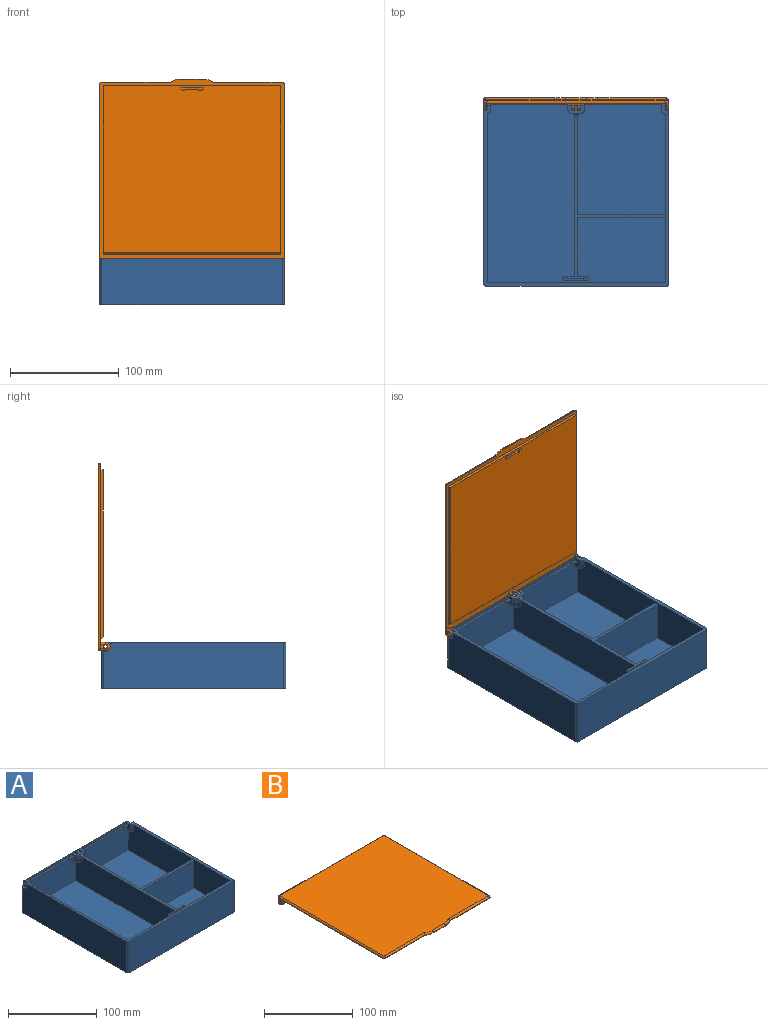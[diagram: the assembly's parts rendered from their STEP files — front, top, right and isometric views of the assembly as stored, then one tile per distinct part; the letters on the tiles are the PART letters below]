
ASSEMBLY  parts=2 mates=1
PART A: 141 faces, bbox 170x170x43 mm
  f0: plane 71.5x2.44mm, normal (0,-1,0), area 170.4mm2, adj f4,f5,f25,f28,f56,f59,f129,f130
  f1: plane 71.5x2.44mm, normal (0,-1,0), area 170.4mm2, adj f6,f7,f26,f27,f57,f60,f125,f126
  f2: plane 80.5x34.56mm, normal (0,-1,0), area 2726.1mm2, adj f4,f5,f25,f28,f32,f34,f44,f56
  f3: plane 80.5x34.56mm, normal (0,-1,0), area 2726.1mm2, adj f6,f7,f26,f27,f33,f39,f43,f57
  f4: cylinder r=1.75mm len=6mm, axis (1,0,0), area 43.1mm2, adj f0,f2,f21,f28,f132
  f5: cylinder r=1.75mm len=61.5mm, axis (1,0,0), area 207.2mm2, adj f0,f2,f130,f131
  f6: cylinder r=1.75mm len=61.5mm, axis (1,0,0), area 207.2mm2, adj f1,f3,f125,f127
  f7: cylinder r=1.75mm len=6mm, axis (1,0,0), area 43.1mm2, adj f1,f3,f22,f26,f126
  f8: plane 9x4mm, normal (0,1,0), area 31.6mm2, adj f13,f15,f38,f100,f101,f102,f105,f106
  f9: plane 20.6x4mm, normal (0,-1,0), area 79.4mm2, adj f11,f12,f15,f90,f91,f92,f96,f97
  f10: plane 20.6x4mm, normal (0,1,0), area 79.4mm2, adj f11,f12,f15,f90,f91,f92,f95,f96
  f11: plane 3.3x1.8mm, normal (0,0,1), area 5.9mm2, adj f9,f10,f90,f98
  f12: plane 11x1.8mm, normal (0,0,1), area 19.8mm2, adj f9,f10,f96,f100
  f13: plane 4.54x4.54mm, normal (0,0.71,-0.71), area 25.7mm2, adj f8,f38,f100,f109
  f14: plane 3.95x3.95mm, normal (0,0.71,-0.71), area 19.6mm2, adj f98,f104,f110,f122,f123
  f15: plane 153.04x95.5mm, normal (0,0,1), area 794.3mm2, adj f8,f9,f10,f16,f32,f34,f38,f39
  f16: plane 164x40mm, normal (0,1,0), area 6185mm2, adj f15,f19,f32,f33,f37,f38,f39,f43
  f17: plane 8.25x8.25mm, normal (1,0,0), area 51.4mm2, adj f20,f31,f36,f51,f54,f58,f61
  f18: plane 8.25x8.25mm, normal (-1,0,0), area 51.4mm2, adj f20,f29,f30,f36,f55,f58,f61
  f19: plane 170x166.13mm, normal (0,0,1), area 1503.5mm2, adj f16,f21,f24,f27,f28,f32,f33,f35
  f20: plane 15x7.13mm, normal (0,0,1), area 76.8mm2, adj f17,f18,f22,f23,f25,f26,f29,f51
  f21: plane 8.25x8.25mm, normal (1,0,0), area 51.4mm2, adj f4,f19,f36,f47,f48,f53,f59
  f22: plane 8.25x8.25mm, normal (1,0,0), area 51.4mm2, adj f7,f20,f29,f30,f36,f55,f60
  f23: plane 8.25x8.25mm, normal (-1,0,0), area 51.4mm2, adj f20,f31,f36,f51,f54,f56,f59
  f24: plane 8.25x8.25mm, normal (-1,0,0), area 51.4mm2, adj f19,f36,f49,f50,f52,f57,f60
  f25: plane 8.25x5mm, normal (1,0,0), area 29.7mm2, adj f0,f2,f20,f56,f59,f80,f82,f84
  f26: plane 8.25x5mm, normal (-1,0,0), area 29.7mm2, adj f1,f3,f7,f20,f60,f74,f76,f77
  f27: plane 9.75x6.5mm, normal (1,0,0), area 48.7mm2, adj f1,f3,f19,f57,f60,f64,f66,f67
  f28: plane 9.75x6.5mm, normal (-1,0,0), area 48.7mm2, adj f0,f2,f4,f19,f59,f68,f70,f71
  f29: plane 4.15x3mm, normal (0,1,0), area 12.4mm2, adj f18,f20,f22,f55
  f30: plane 4.15x3mm, normal (0,0,1), area 12.5mm2, adj f18,f22,f36,f55
  f31: plane 4.15x3mm, normal (0,0,1), area 12.5mm2, adj f17,f23,f36,f54
  f32: plane 164x40mm, normal (-1,0,0), area 6341.9mm2, adj f2,f15,f16,f19,f37,f44,f45,f46
  f33: plane 164x40mm, normal (1,0,0), area 6454.4mm2, adj f3,f16,f19,f43,f62,f63,f65
  f34: plane 101x37.5mm, normal (1,0,0), area 3679.7mm2, adj f2,f15,f44,f46,f81,f83,f85
  f35: plane 166x43mm, normal (-1,0,0), area 7090mm2, adj f19,f42,f49,f50,f52,f113,f116
  f36: plane 166x39.13mm, normal (0,1,0), area 6459.8mm2, adj f17,f18,f21,f22,f23,f24,f30,f31
  f37: plane 80.5x60mm, normal (0,0,1), area 4830mm2, adj f16,f32,f38,f45
  f38: plane 60x37.5mm, normal (1,0,0), area 2207.5mm2, adj f8,f13,f15,f16,f37,f45,f109
  f39: plane 164x37.5mm, normal (-1,0,0), area 5999.7mm2, adj f3,f15,f16,f43,f75,f78,f79,f88
  f40: plane 166x43mm, normal (0,-1,0), area 7138mm2, adj f19,f42,f113,f114
  f41: plane 166x43mm, normal (1,0,0), area 7090mm2, adj f19,f42,f47,f48,f53,f114,f115
  f42: plane 170x170mm, normal (0,0,-1), area 28896.6mm2, adj f35,f36,f40,f41,f113,f114,f115,f116
  f43: plane 164x80.5mm, normal (0,0,1), area 13202mm2, adj f3,f16,f33,f39
  f44: plane 101x80.5mm, normal (0,0,1), area 8130.5mm2, adj f2,f32,f34,f46
  f45: plane 80.5x37.5mm, normal (0,-1,0), area 3018.8mm2, adj f15,f32,f37,f38
  f46: plane 80.5x37.5mm, normal (0,1,0), area 3018.8mm2, adj f15,f32,f34,f44
  f47: plane 4.15x3mm, normal (0,0,1), area 11.6mm2, adj f21,f36,f41,f53,f115
  f48: plane 4.15x3mm, normal (0,1,0), area 12.4mm2, adj f19,f21,f41,f53
  f49: plane 4.15x3mm, normal (0,1,0), area 12.4mm2, adj f19,f24,f35,f52
  f50: plane 4.15x3mm, normal (0,0,1), area 11.6mm2, adj f24,f35,f36,f52,f116
  f51: plane 4.15x3mm, normal (0,1,0), area 12.4mm2, adj f17,f20,f23,f54
  f52: cylinder r=4.1mm len=4.1mm, axis (1,0,0), area 19.3mm2, adj f24,f35,f49,f50
  f53: cylinder r=4.1mm len=4.1mm, axis (1,0,0), area 19.3mm2, adj f21,f41,f47,f48
  f54: cylinder r=4.1mm len=4.1mm, axis (-1,0,0), area 19.3mm2, adj f17,f23,f31,f51
  f55: cylinder r=4.1mm len=4.1mm, axis (-1,0,0), area 19.3mm2, adj f18,f22,f29,f30
  f56: cylinder r=1.75mm len=6mm, axis (1,0,0), area 43.1mm2, adj f0,f2,f23,f25,f129
  f57: cylinder r=1.75mm len=6mm, axis (1,0,0), area 43.1mm2, adj f1,f3,f24,f27,f128
  f58: cylinder r=1.75mm len=3.5mm, axis (1,0,0), area 33mm2, adj f17,f18
  f59: cylinder r=4mm len=77.5mm, axis (-1,0,0), area 404.5mm2, adj f0,f19,f20,f21,f23,f25,f28,f36
  f60: cylinder r=4mm len=77.5mm, axis (-1,0,0), area 404.5mm2, adj f1,f19,f20,f22,f24,f26,f27,f36
  f61: cylinder r=4mm len=3.88mm, axis (-1,0,0), area 18.1mm2, adj f17,f18,f20,f36
  f62: cylinder r=1.5mm len=4.25mm, axis (0,0,-1), area 10mm2, adj f19,f33,f63,f64
  f63: torus R=8.5mm, axis (-1,0,0), area 27.9mm2, adj f33,f62,f65,f66
  f64: cylinder r=1.5mm len=4.25mm, axis (0,0,-1), area 10mm2, adj f19,f27,f62,f66
  f65: cylinder r=1.5mm len=1.5mm, axis (0,-1,0), area 2.4mm2, adj f3,f33,f63,f67
  f66: torus R=5.5mm, axis (1,0,0), area 23.9mm2, adj f27,f63,f64,f67
  f67: cylinder r=1.5mm len=1.5mm, axis (0,-1,0), area 2.4mm2, adj f3,f27,f65,f66
  f68: cylinder r=1.5mm len=1.5mm, axis (0,-1,0), area 2.4mm2, adj f2,f28,f69,f70
  f69: cylinder r=1.5mm len=1.5mm, axis (0,1,0), area 2.4mm2, adj f2,f32,f68,f72
  f70: torus R=5.5mm, axis (-1,0,0), area 23.9mm2, adj f28,f68,f71,f72
  f71: cylinder r=1.5mm len=4.25mm, axis (0,0,1), area 10mm2, adj f19,f28,f70,f73
  f72: torus R=8.5mm, axis (-1,0,0), area 27.9mm2, adj f32,f69,f70,f73
  f73: cylinder r=1.5mm len=4.25mm, axis (0,0,1), area 10mm2, adj f19,f32,f71,f72
  f74: cylinder r=3mm len=3mm, axis (0,1,0), area 4.7mm2, adj f3,f26,f75,f76
  f75: cylinder r=3mm len=3mm, axis (0,-1,0), area 4.7mm2, adj f3,f39,f74,f78
  f76: torus R=4mm, axis (-1,0,0), area 43.7mm2, adj f26,f74,f77,f78
  f77: cylinder r=3mm len=4.25mm, axis (0,0,1), area 20mm2, adj f20,f26,f76,f79
  f78: torus R=10mm, axis (-1,0,0), area 59.9mm2, adj f39,f75,f76,f79
  f79: cylinder r=3mm len=4.25mm, axis (0,0,1), area 13mm2, adj f15,f39,f77,f78,f86
  f80: cylinder r=3mm len=4.25mm, axis (0,0,-1), area 20mm2, adj f20,f25,f81,f82
  f81: cylinder r=3mm len=4.25mm, axis (0,0,-1), area 13mm2, adj f15,f34,f80,f83,f86
  f82: torus R=4mm, axis (-1,0,0), area 43.7mm2, adj f25,f80,f83,f84
  f83: torus R=10mm, axis (-1,0,0), area 59.9mm2, adj f34,f81,f82,f85
  f84: cylinder r=3mm len=3mm, axis (0,1,0), area 4.7mm2, adj f2,f25,f82,f85
  f85: cylinder r=3mm len=3mm, axis (0,-1,0), area 4.7mm2, adj f2,f34,f83,f84
  f86: cylinder r=3mm len=9mm, axis (-1,0,0), area 20.6mm2, adj f15,f20,f79,f81
  f87: plane 6.17x3mm, normal (-1,0,0), area 14mm2, adj f15,f103,f108,f123
  f88: plane 9x4mm, normal (0,1,0), area 31.6mm2, adj f15,f39,f94,f96,f97,f98,f103,f104
  f89: plane 6.17x3mm, normal (1,0,0), area 14mm2, adj f15,f105,f107,f118
  f90: plane 4x1.8mm, normal (1,0,0), area 7.2mm2, adj f9,f10,f11,f15
  f91: plane 4x1.8mm, normal (-1,0,0), area 7.2mm2, adj f9,f10,f15,f92
  f92: plane 3.3x1.8mm, normal (0,0,1), area 5.9mm2, adj f9,f10,f91,f102
  f93: plane 3.95x3.95mm, normal (0,0.71,-0.71), area 19.6mm2, adj f102,f106,f112,f118,f119
  f94: plane 4.54x4.54mm, normal (0,0.71,-0.71), area 25.7mm2, adj f39,f88,f96,f111
  f95: plane 2.25x1.5mm, normal (0,0,-1), area 3.4mm2, adj f10,f16,f96,f98
  f96: plane 9.07x6mm, normal (-1,0,0), area 22.7mm2, adj f9,f10,f12,f16,f88,f94,f95,f97
  f97: plane 1.95x1.5mm, normal (0,0,-1), area 2.9mm2, adj f9,f88,f96,f98
  f98: plane 9.07x6mm, normal (1,0,0), area 22.7mm2, adj f9,f10,f11,f14,f16,f88,f95,f97
  f99: plane 2.25x1.5mm, normal (0,0,-1), area 3.4mm2, adj f10,f16,f100,f102
  f100: plane 9.07x6mm, normal (1,0,0), area 22.7mm2, adj f8,f9,f10,f12,f13,f16,f99,f101
  f101: plane 1.95x1.5mm, normal (0,0,-1), area 2.9mm2, adj f8,f9,f100,f102
  f102: plane 9.07x6mm, normal (-1,0,0), area 22.7mm2, adj f8,f9,f10,f16,f92,f93,f99,f101
  f103: cylinder r=2mm len=3.17mm, axis (0,0,-1), area 10mm2, adj f15,f87,f88,f124
  f104: cylinder r=2mm len=3.5mm, axis (-1,0,0), area 5.5mm2, adj f14,f88,f98,f124
  f105: cylinder r=2mm len=3.17mm, axis (0,0,1), area 10mm2, adj f8,f15,f89,f117
  f106: cylinder r=2mm len=3.5mm, axis (-1,0,0), area 5.5mm2, adj f8,f93,f102,f117
  f107: cylinder r=1mm len=12.07mm, axis (0,0,-1), area 14.1mm2, adj f15,f16,f89,f119,f120
  f108: cylinder r=1mm len=12.07mm, axis (0,0,1), area 14.1mm2, adj f15,f16,f87,f121,f122
  f109: cylinder r=5mm len=4mm, axis (1,0,0), area 15.7mm2, adj f13,f16,f38,f100
  f110: cylinder r=5mm len=6.5mm, axis (1,0,0), area 19.9mm2, adj f14,f16,f98,f121
  f111: cylinder r=5mm len=4mm, axis (1,0,0), area 15.7mm2, adj f16,f39,f94,f96
  f112: cylinder r=5mm len=6.5mm, axis (1,0,0), area 19.9mm2, adj f16,f93,f102,f120
  f113: cylinder r=2mm len=43mm, axis (0,0,1), area 135.1mm2, adj f19,f35,f40,f42
  f114: cylinder r=2mm len=43mm, axis (0,0,-1), area 135.1mm2, adj f19,f40,f41,f42
  f115: cylinder r=2mm len=34.75mm, axis (0,0,1), area 109.2mm2, adj f36,f41,f42,f47
  f116: cylinder r=2mm len=34.75mm, axis (0,0,-1), area 109.2mm2, adj f35,f36,f42,f50
  f117: sphere r=2mm, area 3.1mm2, adj f105,f106,f118
  f118: cylinder r=2mm len=4.41mm, axis (0,0.71,0.71), area 13.3mm2, adj f89,f93,f117,f119
  f119: bspline ~2.36x2.05mm, area 3.1mm2, adj f93,f107,f118,f120
  f120: bspline ~5.61x3mm, area 6.1mm2, adj f107,f112,f119
  f121: bspline ~5.44x2.98mm, area 5.4mm2, adj f108,f110,f122
  f122: bspline ~2.36x2.05mm, area 3.1mm2, adj f14,f108,f121,f123
  f123: cylinder r=2mm len=4.41mm, axis (0,0.71,0.71), area 13.3mm2, adj f14,f87,f122,f124
  f124: sphere r=2mm, area 3.1mm2, adj f103,f104,f123
  f125: plane 4.87x1.5mm, normal (1,0,0), area 3.7mm2, adj f1,f3,f6,f133,f134
  f126: plane 4.87x1.5mm, normal (-1,0,0), area 3.7mm2, adj f1,f3,f7,f133,f134
  f127: plane 4.87x1.5mm, normal (-1,0,0), area 3.7mm2, adj f1,f3,f6,f135,f136
  f128: plane 4.87x1.5mm, normal (1,0,0), area 3.7mm2, adj f1,f3,f57,f135,f136
  f129: plane 4.87x1.5mm, normal (1,0,0), area 3.7mm2, adj f0,f2,f56,f139,f140
  f130: plane 4.87x1.5mm, normal (-1,0,0), area 3.7mm2, adj f0,f2,f5,f139,f140
  f131: plane 4.87x1.5mm, normal (1,0,0), area 3.7mm2, adj f0,f2,f5,f137,f138
  f132: plane 4.87x1.5mm, normal (-1,0,0), area 3.7mm2, adj f0,f2,f4,f137,f138
  f133: cylinder r=2.8mm len=2.44mm, axis (1,0,0), area 6mm2, adj f3,f125,f126,f134
  f134: cylinder r=2.8mm len=2.44mm, axis (1,0,0), area 6mm2, adj f1,f125,f126,f133
  f135: cylinder r=2.8mm len=2.44mm, axis (1,0,0), area 6mm2, adj f1,f127,f128,f136
  f136: cylinder r=2.8mm len=2.44mm, axis (1,0,0), area 6mm2, adj f3,f127,f128,f135
  f137: cylinder r=2.8mm len=2.44mm, axis (1,0,0), area 6mm2, adj f0,f131,f132,f138
  f138: cylinder r=2.8mm len=2.44mm, axis (1,0,0), area 6mm2, adj f2,f131,f132,f137
  f139: cylinder r=2.8mm len=2.44mm, axis (1,0,0), area 6mm2, adj f0,f129,f130,f140
  f140: cylinder r=2.8mm len=2.44mm, axis (1,0,0), area 6mm2, adj f2,f129,f130,f139
PART B: 69 faces, bbox 170x175x11.3 mm
  f0: plane 12.6x4mm, normal (0,1,0), area 50.4mm2, adj f4,f13,f16,f17
  f1: plane 4x1.6mm, normal (0,1,0), area 6.4mm2, adj f4,f12,f13,f16
  f2: plane 12.6x4mm, normal (0,-1,0), area 50.4mm2, adj f4,f13,f14,f15
  f3: plane 4x1.35mm, normal (0,-1,0), area 5.4mm2, adj f4,f13,f14,f68
  f4: plane 163.5x153.55mm, normal (0,0,-1), area 25064.4mm2, adj f0,f1,f2,f3,f5,f6,f7,f8
  f5: plane 163.5x2.5mm, normal (0,-1,0), area 408.7mm2, adj f4,f6,f7,f19
  f6: plane 155.55x2.5mm, normal (-1,0,0), area 386.9mm2, adj f4,f5,f8,f18,f19
  f7: plane 155.55x2.5mm, normal (1,0,0), area 386.9mm2, adj f4,f5,f8,f18,f19
  f8: plane 163.5x2mm, normal (0,0.71,-0.71), area 462.4mm2, adj f4,f6,f7,f18
  f9: plane 4x1.6mm, normal (0,1,0), area 6.4mm2, adj f4,f10,f13,f17
  f10: plane 4x1.55mm, normal (1,0,0), area 6.2mm2, adj f4,f9,f13,f67
  f11: plane 4x1.35mm, normal (0,-1,0), area 5.4mm2, adj f4,f13,f15,f67
  f12: plane 4x1.55mm, normal (-1,0,0), area 6.2mm2, adj f1,f4,f13,f68
  f13: plane 20.6x3mm, normal (0,0,-1), area 41mm2, adj f0,f1,f2,f3,f9,f10,f11,f12
  f14: cylinder r=1.5mm len=4mm, axis (0,0,-1), area 11.1mm2, adj f2,f3,f4,f13
  f15: cylinder r=1.5mm len=4mm, axis (0,0,-1), area 11.1mm2, adj f2,f4,f11,f13
  f16: cylinder r=1.5mm len=4mm, axis (0,0,-1), area 11.1mm2, adj f0,f1,f4,f13
  f17: cylinder r=1.5mm len=4mm, axis (0,0,-1), area 11.1mm2, adj f0,f4,f9,f13
  f18: plane 163.5x0.5mm, normal (0,1,0), area 81.8mm2, adj f6,f7,f8,f19
  f19: plane 173x170mm, normal (0,0,-1), area 3477.6mm2, adj f5,f6,f7,f18,f45,f46,f47,f48
  f20: sphere r=2mm, area 6.3mm2, adj f29,f39,f40
  f21: sphere r=2mm, area 6.3mm2, adj f27,f40,f41
  f22: plane 169x166mm, normal (0,0,1), area 27653.3mm2, adj f27,f29,f31,f34,f35,f40,f43,f44
  f23: cylinder r=1.75mm len=3.5mm, axis (1,0,0), area 30.8mm2, adj f61,f63
  f24: cylinder r=1.75mm len=3.5mm, axis (1,0,0), area 30.8mm2, adj f58,f60
  f25: cylinder r=1.75mm len=3.5mm, axis (1,0,0), area 30.8mm2, adj f53,f64
  f26: torus R=2mm, axis (-1,0,0), area 32.3mm2, adj f41,f42,f53,f66
  f27: cylinder r=2mm len=166mm, axis (0,1,0), area 521.5mm2, adj f21,f22,f32,f53
  f28: cylinder r=1.75mm len=3.5mm, axis (1,0,0), area 30.8mm2, adj f52,f57
  f29: cylinder r=2mm len=166mm, axis (0,-1,0), area 521.5mm2, adj f20,f22,f33,f52
  f30: torus R=2mm, axis (-1,0,0), area 32.3mm2, adj f38,f39,f52,f54
  f31: cylinder r=2mm len=18.93mm, axis (1,0,0), area 59.5mm2, adj f22,f43,f44,f51
  f32: sphere r=2mm, area 6.3mm2, adj f27,f34,f50
  f33: sphere r=2mm, area 6.3mm2, adj f29,f35,f47
  f34: cylinder r=2mm len=63.59mm, axis (-1,0,0), area 198.6mm2, adj f22,f32,f43,f49
  f35: cylinder r=2mm len=63.59mm, axis (-1,0,0), area 198.6mm2, adj f22,f33,f44,f46
  f36: cylinder r=4mm len=8mm, axis (1,0,0), area 35.2mm2, adj f56,f61,f62,f63
  f37: cylinder r=4mm len=8mm, axis (1,0,0), area 35.2mm2, adj f56,f58,f59,f60
  f38: cylinder r=4mm len=8mm, axis (1,0,0), area 10.1mm2, adj f30,f55,f56,f57
  f39: cylinder r=2mm len=5mm, axis (0,0,1), area 15.7mm2, adj f20,f30,f52,f56
  f40: cylinder r=2mm len=166mm, axis (1,0,0), area 521.5mm2, adj f20,f21,f22,f56
  f41: cylinder r=2mm len=5mm, axis (0,0,-1), area 15.7mm2, adj f21,f26,f53,f56
  f42: cylinder r=4mm len=8mm, axis (1,0,0), area 10.1mm2, adj f26,f56,f64,f65
  f43: torus R=18mm, axis (0,0,1), area 34.2mm2, adj f22,f31,f34,f48
  f44: torus R=18mm, axis (0,0,1), area 34.2mm2, adj f22,f31,f35,f45
  f45: cylinder r=20mm len=10.54mm, axis (0,0,1), area 5.5mm2, adj f19,f44,f46,f51
  f46: plane 63x0.5mm, normal (0,-1,0), area 31.5mm2, adj f19,f35,f45,f47
  f47: cylinder r=2mm len=2mm, axis (0,0,-1), area 1.6mm2, adj f19,f33,f46,f52
  f48: cylinder r=20mm len=10.54mm, axis (0,0,1), area 5.5mm2, adj f19,f43,f49,f51
  f49: plane 63x0.5mm, normal (0,-1,0), area 31.5mm2, adj f19,f34,f48,f50
  f50: cylinder r=2mm len=2mm, axis (0,0,1), area 1.6mm2, adj f19,f32,f49,f53
  f51: plane 18.93x0.5mm, normal (0,-1,0), area 9.5mm2, adj f19,f31,f45,f48
  f52: plane 166x7mm, normal (1,0,0), area 97.7mm2, adj f19,f28,f29,f30,f39,f47,f54
  f53: plane 166x7mm, normal (-1,0,0), area 97.7mm2, adj f19,f25,f26,f27,f41,f50,f66
  f54: cylinder r=2mm len=4.5mm, axis (0,0,-1), area 14.1mm2, adj f19,f30,f52,f55
  f55: plane 4.5x0.8mm, normal (0,-1,0), area 3.6mm2, adj f19,f38,f54,f57
  f56: plane 166x5mm, normal (0,1,0), area 115.4mm2, adj f19,f36,f37,f38,f39,f40,f41,f42
  f57: plane 8.5x8mm, normal (-1,0,0), area 51.5mm2, adj f19,f28,f38,f55,f56
  f58: plane 8.5x8mm, normal (1,0,0), area 51.5mm2, adj f19,f24,f37,f56,f59
  f59: plane 4.5x2.8mm, normal (0,-1,0), area 12.6mm2, adj f19,f37,f58,f60
  f60: plane 8.5x8mm, normal (-1,0,0), area 51.5mm2, adj f19,f24,f37,f56,f59
  f61: plane 8.5x8mm, normal (1,0,0), area 51.5mm2, adj f19,f23,f36,f56,f62
  f62: plane 4.5x2.8mm, normal (0,-1,0), area 12.6mm2, adj f19,f36,f61,f63
  f63: plane 8.5x8mm, normal (-1,0,0), area 51.5mm2, adj f19,f23,f36,f56,f62
  f64: plane 8.5x8mm, normal (1,0,0), area 51.5mm2, adj f19,f25,f42,f56,f65
  f65: plane 4.5x0.8mm, normal (0,-1,0), area 3.6mm2, adj f19,f42,f64,f66
  f66: cylinder r=2mm len=4.5mm, axis (0,0,1), area 14.1mm2, adj f19,f26,f53,f65
  f67: plane 4x0.25mm, normal (0.71,-0.71,0), area 1.4mm2, adj f4,f10,f11,f13
  f68: plane 4x0.25mm, normal (-0.71,-0.71,0), area 1.4mm2, adj f3,f4,f12,f13
PLACE A t=(13.28,-112.16,60.85)mm
PLACE B rot(axis=(-1,0,0),90deg) t=(13.08,14.84,265.85)mm
MATE revolute B.f26 <-> A.f59  axis (-1,0,0) through (180.28,53.84,99.85)mm
